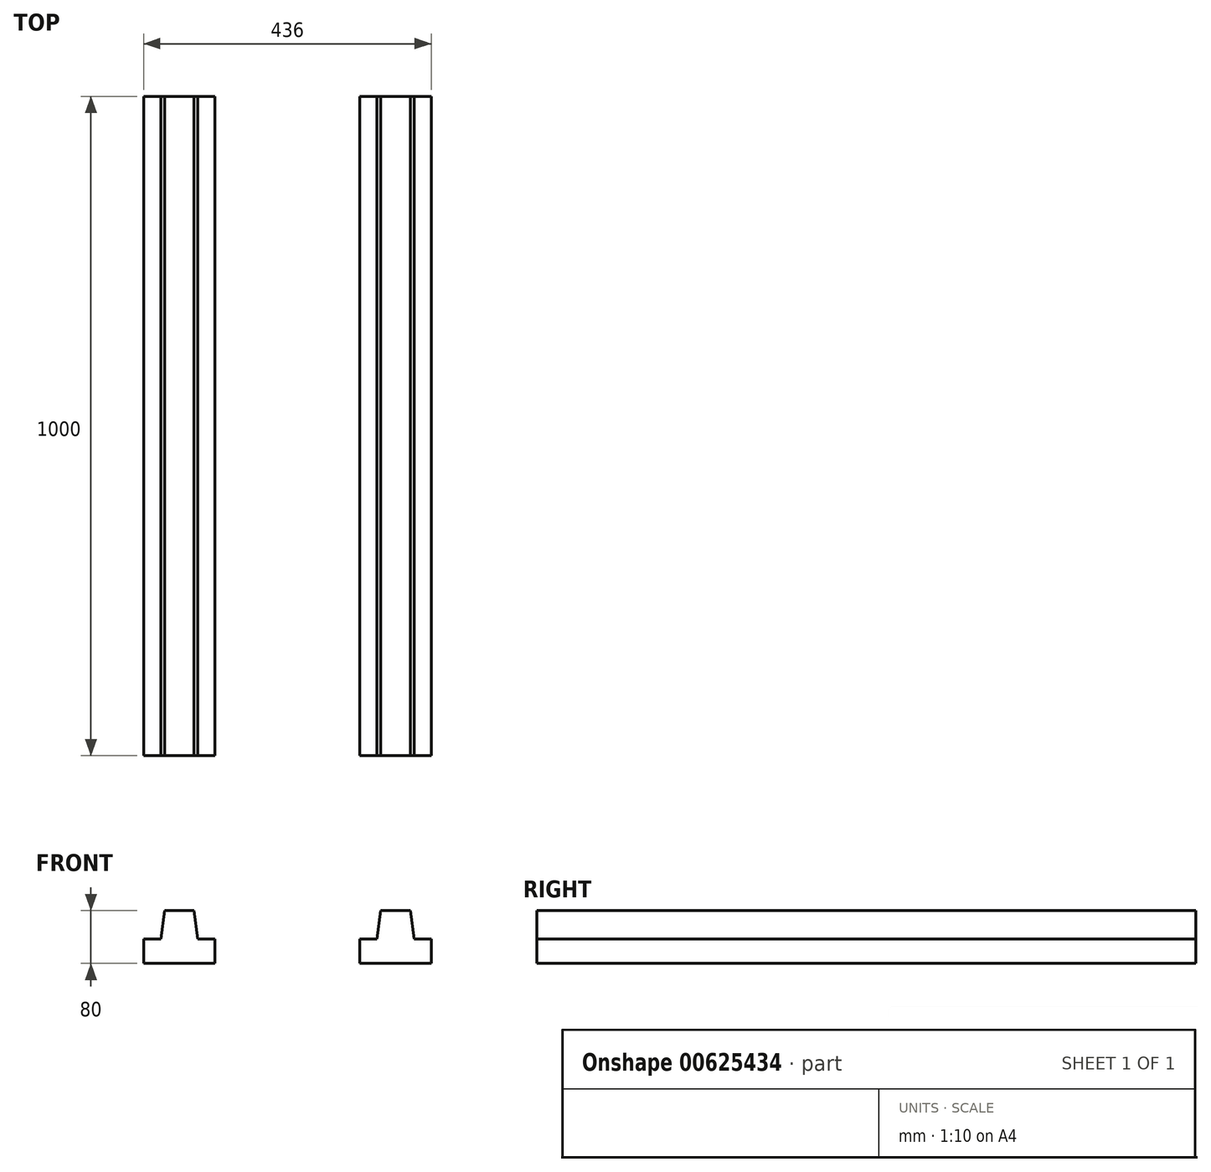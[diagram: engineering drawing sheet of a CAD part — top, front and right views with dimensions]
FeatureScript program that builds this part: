
annotation { "Feature Type Name" : "Feature", "Feature Type Description" : "" }
export const myFeature = defineFeature(function(context is Context, id is Id, definition is map)
    precondition{}
    {
        {
            var Q0;
            Q0=qCreatedBy(makeId("Front.planeOp"),FACE);
            var sketch = newSketch(context, id + "F0", { "sketchPlane" : qUnion([Q0])});
            skLineSegment(sketch, "E0.bottom", {"start": v(0, 0) * mm, "end": v(108, 0) * mm});
            skLineSegment(sketch, "E0.top", {"start": v(31.5, 80) * mm, "end": v(76.5, 80) * mm});
            skLineSegment(sketch, "E0.left", {"start": v(0, 0) * mm, "end": v(0, 37) * mm});
            skLineSegment(sketch, "E0.right", {"start": v(108, 0) * mm, "end": v(108, 37) * mm});
            skLineSegment(sketch, "E1", {"start": v(108, 37) * mm, "end": v(82, 37) * mm});
            skLineSegment(sketch, "E2", {"start": v(0, 37) * mm, "end": v(26, 37) * mm});
            skLineSegment(sketch, "E3", {"start": v(54, 80) * mm, "end": v(76.5, 80) * mm});
            skLineSegment(sketch, "E4", {"start": v(76.5, 80) * mm, "end": v(82, 37) * mm});
            skLineSegment(sketch, "E5", {"start": v(54, 80) * mm, "end": v(31.5, 80) * mm});
            skLineSegment(sketch, "E6", {"start": v(31.5, 80) * mm, "end": v(26, 37) * mm});
            skPoint(sketch, "E7.orphan", {"position": v(0, 80) * mm});
            skPoint(sketch, "E8.orphan", {"position": v(108, 80) * mm});
            skSolve(sketch);
        }
        {
            var Q0;
            Q0 = qSketchRegion(id + "F0", true);
            extrude(context, id + "F1", {"entities" : qUnion([Q0]), "oppositeDirection" : true, "depth" : 1000 * mm, "offsetDistance" : 25 * mm});
        }
        {
            var Q0;
            Q0=qCreatedBy(makeId("Right.planeOp"),FACE);
            cPlane(context, id + "F2", {"entities" : qUnion([Q0]), "cplaneType" : CPlaneType.OFFSET, "offset" : 110 * mm, "oppositeDirection" : true, "width" : 150 * mm, "height" : 150 * mm});
        }
        {
            var Q0;
            Q0=makeQuery(id+"F1.opExtrude","SWEPT_BODY",BODY,{"disambiguationData":[OSD([sQuery(id+"F0.wireOp",EDGE,"E0.bottom"),sQuery(id+"F0.wireOp",EDGE,"E0.left"),sQuery(id+"F0.wireOp",EDGE,"E0.right"),sQuery(id+"F0.wireOp",EDGE,"E1"),sQuery(id+"F0.wireOp",EDGE,"E2"),sQuery(id+"F0.wireOp",EDGE,"E3"),sQuery(id+"F0.wireOp",EDGE,"E4"),sQuery(id+"F0.wireOp",EDGE,"E5"),sQuery(id+"F0.wireOp",EDGE,"E6")])]});
            var Q1;
            Q1=qCreatedBy(id+"F2.planeOp",FACE);
            mirror(context, id + "F3", {"entities" : qUnion([Q0]), "mirrorPlane" : qUnion([Q1])});
        }
    });
